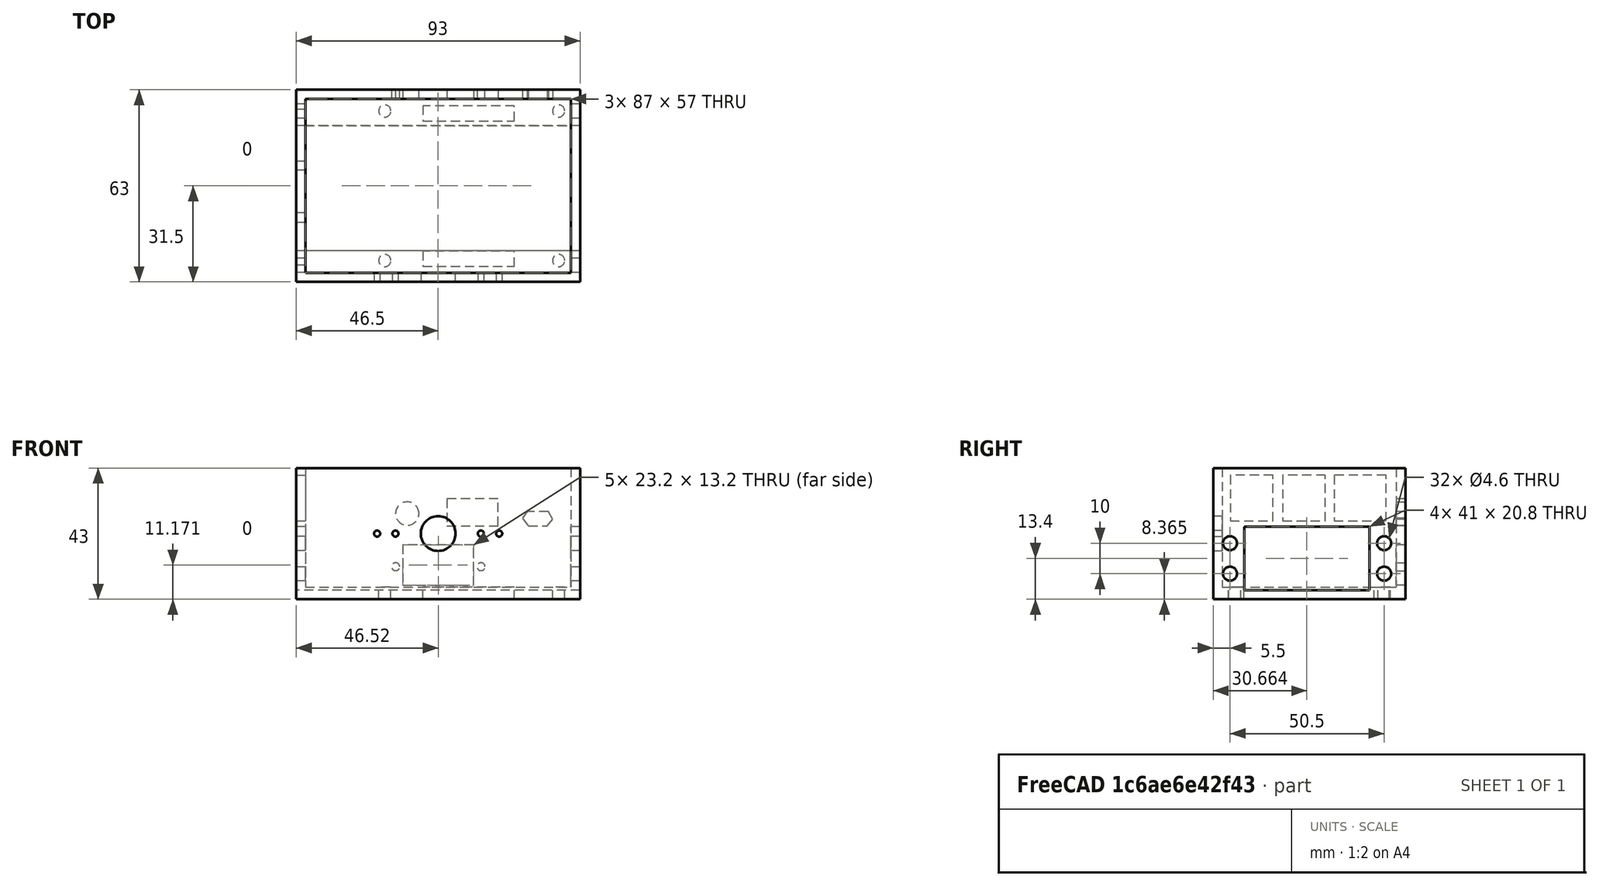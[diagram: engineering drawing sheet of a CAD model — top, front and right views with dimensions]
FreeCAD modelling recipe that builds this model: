
FCSTD DOCUMENT  (FreeCAD 0.17R8939 (Git))
Label: tronco
License: All rights reserved
LicenseURL: http://en.wikipedia.org/wiki/All_rights_reserved
objects: Sketcher::SketchObject×6, PartDesign::Pocket×6, Mesh::Feature×5, Part::Cylinder×4, App::MeasureDistance×3, App::DocumentObjectGroup×2, Part::Box×1, Part::MultiFuse×1, Part::Cut×1
note: 25 computed .brp shape members not serialized (recipe doc carries the construction recipe); baked Part::Feature solids carry a one-line shape summary decoded from their .brp

FEATURE [Mesh::Feature] rPi2_01
FEATURE [Mesh::Feature] Parallax_servo_repaired
  Placement = pos=(62,0,-22) rot=(0.57735,0.57735,0.57735;2.0944rad)
FEATURE [Mesh::Feature] Parallax_servo_repaired001
  Placement = pos=(22,0,-2) rot=(0.57735,0.57735,-0.57735;4.18879rad)
FEATURE [Mesh::Feature] Servo_SG90
  Placement = pos=(31,44,-7) rot=(-1,0,0;1.5708rad)
FEATURE [Part::Box] Box  label="Cubo"
  AttacherType = Attacher::AttachEngine3D
  Height = 43
  Length = 93
  Placement = pos=(-5,-3,-25) rot=(0,0,1;0rad)
  Width = 63
FEATURE [Sketcher::SketchObject] Sketch
  ExternalGeometry = -> [Box]
  MapMode = 5
  Placement = pos=(-5,-3,18) rot=(0,0,1;0rad)
  Support = -> [Box]
  sketch-geometry (4):
    g0: LineSegment StartX=3 StartY=60 StartZ=0 EndX=90 EndY=60 EndZ=0
    g1: LineSegment StartX=90 StartY=60 StartZ=0 EndX=90 EndY=3 EndZ=0
    g2: LineSegment StartX=90 StartY=3 StartZ=0 EndX=3 EndY=3 EndZ=0
    g3: LineSegment StartX=3 StartY=3 StartZ=0 EndX=3 EndY=60 EndZ=0
  constraints (12):
    c: Coincident(g0,g1)
    c: Coincident(g1,g2)
    c: Coincident(g2,g3)
    c: Coincident(g3,g0)
    c: Horizontal(g0)
    c: Horizontal(g2)
    c: Vertical(g1)
    c: Vertical(g3)
    c: Distance(g0,g-3) = 3
    c: Distance(g0,g-4) = 3
    c: DistanceY(g-1,g1) = 3
    c: DistanceX(g-2,g2) = 3
FEATURE [PartDesign::Pocket] Pocket  label="Puertos Multimedia"
  Length = 39
  Placement = pos=(-5,-3,-25) rot=(0,0,1;0rad)
  Profile = -> Sketch
  Type = 0
FEATURE [Sketcher::SketchObject] Sketch001
  ExternalGeometry = -> [Pocket]
  MapMode = 5
  Placement = pos=(-5,60,-25) rot=(0,0.707107,0.707107;3.14159rad)
  Support = -> [Pocket]
  sketch-geometry (18):
    g0: Circle CenterX=-36.37 CenterY=28.0687 CenterZ=0 NormalX=0 NormalY=0 NormalZ=1 Radius=3.84
    g1: LineSegment StartX=-66.2 StartY=32.9 StartZ=0 EndX=-49.42 EndY=32.9 EndZ=0
    g2: LineSegment StartX=-49.42 StartY=32.9 StartZ=0 EndX=-49.42 EndY=24.05 EndZ=0
    g3: LineSegment StartX=-49.42 StartY=24.05 StartZ=0 EndX=-66.2 EndY=24.05 EndZ=0
    g4: LineSegment StartX=-66.2 StartY=24.05 StartZ=0 EndX=-66.2 EndY=32.9 EndZ=0
    g5: LineSegment StartX=-82.6171 StartY=28.7 StartZ=0 EndX=-75.6871 EndY=28.7 EndZ=0
    g6: LineSegment StartX=-75.6871 StartY=28.7 StartZ=0 EndX=-74.1347 EndY=26.5182 EndZ=0
    g7: LineSegment StartX=-74.1347 StartY=26.5182 StartZ=0 EndX=-76.0497 EndY=24.0555 EndZ=0
    g8: LineSegment StartX=-76.0497 StartY=24.0555 StartZ=0 EndX=-82.2523 EndY=24.0555 EndZ=0
    g9: LineSegment StartX=-82.2523 StartY=24.0555 StartZ=0 EndX=-84.08 EndY=26.1498 EndZ=0
    g10: LineSegment StartX=-84.08 StartY=26.1498 StartZ=0 EndX=-82.6171 EndY=28.7 EndZ=0
    g11: LineSegment StartX=-58.12 StartY=17.7713 StartZ=0 EndX=-34.92 EndY=17.7713 EndZ=0
    g12: LineSegment StartX=-34.92 StartY=17.7713 StartZ=0 EndX=-34.92 EndY=4.57128 EndZ=0
    g13: LineSegment StartX=-34.92 StartY=4.57128 StartZ=0 EndX=-58.12 EndY=4.57128 EndZ=0
    g14: LineSegment StartX=-58.12 StartY=4.57128 StartZ=0 EndX=-58.12 EndY=17.7713 EndZ=0
    g15: Circle CenterX=-32.57 CenterY=10.65 CenterZ=0 NormalX=0 NormalY=0 NormalZ=1 Radius=1.3
    g16: Circle CenterX=-60.57 CenterY=10.65 CenterZ=0 NormalX=0 NormalY=0 NormalZ=1 Radius=1.3
    g17: LineSegment [constr] StartX=-93 StartY=10.65 StartZ=0 EndX=0 EndY=10.65 EndZ=0
  constraints (48):
    c: Coincident(g1,g2)
    c: Coincident(g2,g3)
    c: Coincident(g3,g4)
    c: Coincident(g4,g1)
    c: Horizontal(g1)
    c: Horizontal(g3)
    c: Vertical(g2)
    c: Vertical(g4)
    c: Horizontal(g5)
    c: Coincident(g5,g6)
    c: Coincident(g6,g7)
    c: Coincident(g7,g8)
    c: Horizontal(g8)
    c: Coincident(g8,g9)
    c: Coincident(g9,g10)
    c: Coincident(g10,g5)
    c: Coincident(g11,g12)
    c: Coincident(g12,g13)
    c: Coincident(g13,g14)
    c: Coincident(g14,g11)
    c: Horizontal(g11)
    c: Horizontal(g13)
    c: Vertical(g12)
    c: Vertical(g14)
    c: DistanceX(g13,g13) = 23.2
    c: DistanceY(g12,g12) = 13.2
    c: Horizontal(g17)
    c: PointOnObject(g16,g17)
    c: PointOnObject(g15,g17)
    c: Radius(g16) = 1.3
    c: Equal(g15,g16)
    c: PointOnObject(g17,g-2)
    c: PointOnObject(g17,g-3)
    c: Distance(g16,g15) = 28
    c: Distance(g9,g-3) = 8.92
    c: DistanceX(g5,g5) = 6.93
    c: Distance(g5,g9) = 2.94
    c: Distance(g5,g-4) = 14.3
    c: DistanceX(g1,g1) = 16.78
    c: DistanceY(g2,g2) = 8.85
    c: Distance(g1,g-4) = 10.1
    c: Distance(g3,g-3) = 26.8
    c: Radius(g0) = 3.84
    c: DistanceX(g-2,g0) = -36.37
    c: Distance(g13,g-3) = 34.88
    c: Distance(g15,g12) = 2.35
    c: Angle(g7,g8) = 2.23175
    c: Distance(g-1,g17) = 10.65
FEATURE [PartDesign::Pocket] Pocket001  label="Servomotores"
  Length = 5
  Placement = pos=(-5,-3,-25) rot=(0,0,1;0rad)
  Profile = -> Sketch001
  Type = 0
FEATURE [Sketcher::SketchObject] Sketch002
  ExternalGeometry = -> [Pocket001]
  MapMode = 5
  Placement = pos=(88,-3,-25) rot=(0.57735,0.57735,0.57735;2.0944rad)
  Support = -> [Pocket001]
  sketch-geometry (12):
    g0: LineSegment StartX=10.1642 StartY=23.8 StartZ=0 EndX=51.1642 EndY=23.8 EndZ=0
    g1: LineSegment StartX=51.1642 StartY=23.8 StartZ=0 EndX=51.1642 EndY=3 EndZ=0
    g2: LineSegment StartX=51.1642 StartY=3 StartZ=0 EndX=10.1642 EndY=3 EndZ=0
    g3: LineSegment StartX=10.1642 StartY=3 StartZ=0 EndX=10.1642 EndY=23.8 EndZ=0
    g4: Circle CenterX=56 CenterY=18.3651 CenterZ=0 NormalX=0 NormalY=0 NormalZ=1 Radius=2.3
    g5: Circle CenterX=56 CenterY=8.36507 CenterZ=0 NormalX=0 NormalY=0 NormalZ=1 Radius=2.3
    g6: Circle CenterX=5.5 CenterY=18.3651 CenterZ=0 NormalX=0 NormalY=0 NormalZ=1 Radius=2.3
    g7: Circle CenterX=5.5 CenterY=8.36507 CenterZ=0 NormalX=0 NormalY=0 NormalZ=1 Radius=2.3
    g8: LineSegment [constr] StartX=5.5 StartY=18.3651 StartZ=0 EndX=56 EndY=18.3651 EndZ=0
    g9: LineSegment [constr] StartX=56 StartY=18.3651 StartZ=0 EndX=56 EndY=8.36507 EndZ=0
    g10: LineSegment [constr] StartX=56 StartY=8.36507 StartZ=0 EndX=5.5 EndY=8.36507 EndZ=0
    g11: LineSegment [constr] StartX=5.5 StartY=8.36507 StartZ=0 EndX=5.5 EndY=18.3651 EndZ=0
  constraints (32):
    c: Coincident(g0,g1)
    c: Coincident(g1,g2)
    c: Coincident(g2,g3)
    c: Coincident(g3,g0)
    c: Horizontal(g0)
    c: Horizontal(g2)
    c: Vertical(g1)
    c: Vertical(g3)
    c: DistanceX(g0,g0) = 41
    c: DistanceY(g1,g1) = 20.8
    c: Radius(g5) = 2.3
    c: Equal(g5,g4)
    c: Equal(g4,g6)
    c: Equal(g6,g7)
    c: Coincident(g8,g9)
    c: Coincident(g9,g10)
    c: Coincident(g10,g11)
    c: Coincident(g11,g8)
    c: Horizontal(g8)
    c: Horizontal(g10)
    c: Vertical(g9)
    c: Vertical(g11)
    c: Coincident(g7,g10)
    c: Coincident(g6,g8)
    c: Coincident(g4,g8)
    c: Coincident(g5,g9)
    c: DistanceX(g10,g10) = 50.5
    c: DistanceY(g11,g11) = 10
    c: DistanceY(g-1,g7) = 8.36507
    c: Distance(g4,g-3) = 7
    c: DistanceY(g-1,g1) = 3
    c: Distance(g0,g-3) = 11.8358
FEATURE [PartDesign::Pocket] Pocket002  label="puertosUSB"
  Length = 5
  Placement = pos=(-5,-3,-25) rot=(0,0,1;0rad)
  Profile = -> Sketch002
  Type = 1
FEATURE [Sketcher::SketchObject] Sketch003
  ExternalGeometry = -> [Pocket002]
  MapMode = 5
  Placement = pos=(-5,-3,-25) rot=(0.57735,-0.57735,-0.57735;2.0944rad)
  Support = -> [Pocket002]
  sketch-geometry (13):
    g0: LineSegment StartX=-19.56 StartY=40.62 StartZ=0 EndX=-5.56 EndY=40.62 EndZ=0
    g1: LineSegment StartX=-5.56 StartY=40.62 StartZ=0 EndX=-5.56 EndY=25.62 EndZ=0
    g2: LineSegment StartX=-5.56 StartY=25.62 StartZ=0 EndX=-19.56 EndY=25.62 EndZ=0
    g3: LineSegment StartX=-19.56 StartY=25.62 StartZ=0 EndX=-19.56 EndY=40.62 EndZ=0
    g4: LineSegment StartX=-36.75 StartY=40.62 StartZ=0 EndX=-22.75 EndY=40.62 EndZ=0
    g5: LineSegment StartX=-22.75 StartY=40.62 StartZ=0 EndX=-22.75 EndY=25.62 EndZ=0
    g6: LineSegment StartX=-22.75 StartY=25.62 StartZ=0 EndX=-36.75 EndY=25.62 EndZ=0
    g7: LineSegment StartX=-36.75 StartY=25.62 StartZ=0 EndX=-36.75 EndY=40.62 EndZ=0
    g8: LineSegment StartX=-56.62 StartY=40.62 StartZ=0 EndX=-39.62 EndY=40.62 EndZ=0
    g9: LineSegment StartX=-39.62 StartY=40.62 StartZ=0 EndX=-39.62 EndY=25.62 EndZ=0
    g10: LineSegment StartX=-39.62 StartY=25.62 StartZ=0 EndX=-56.62 EndY=25.62 EndZ=0
    g11: LineSegment StartX=-56.62 StartY=25.62 StartZ=0 EndX=-56.62 EndY=40.62 EndZ=0
    g12: LineSegment [constr] StartX=-63 StartY=25.62 StartZ=0 EndX=0 EndY=25.62 EndZ=0
  constraints (42):
    c: Coincident(g0,g1)
    c: Coincident(g1,g2)
    c: Coincident(g2,g3)
    c: Coincident(g3,g0)
    c: Horizontal(g0)
    c: Horizontal(g2)
    c: Vertical(g1)
    c: Vertical(g3)
    c: Coincident(g4,g5)
    c: Coincident(g5,g6)
    c: Coincident(g6,g7)
    c: Coincident(g7,g4)
    c: Horizontal(g4)
    c: Horizontal(g6)
    c: Vertical(g5)
    c: Vertical(g7)
    c: Coincident(g8,g9)
    c: Coincident(g9,g10)
    c: Coincident(g10,g11)
    c: Coincident(g11,g8)
    c: Horizontal(g8)
    c: Horizontal(g10)
    c: Vertical(g9)
    c: Vertical(g11)
    c: DistanceY(g1,g1) = 15
    c: DistanceX(g0,g0) = 14
    c: DistanceX(g8,g8) = 17
    c: Equal(g4,g0)
    c: Equal(g9,g7)
    c: Equal(g7,g11)
    c: Equal(g11,g3)
    c: Equal(g3,g1)
    c: Horizontal(g12)
    c: PointOnObject(g12,g-2)
    c: PointOnObject(g12,g-3)
    c: PointOnObject(g10,g12)
    c: PointOnObject(g6,g12)
    c: PointOnObject(g2,g12)
    c: Distance(g4,g0) = 3.19
    c: Distance(g8,g4) = 2.87
    c: Distance(g-3,g12) = 17.38
    c: Distance(g12,g10) = 6.38
FEATURE [PartDesign::Pocket] Pocket003
  Length = 5
  Placement = pos=(-5,-3,-25) rot=(0,0,1;0rad)
  Profile = -> Sketch003
  Type = 0
FEATURE [Part::Cylinder] Cylinder  label="Cilindro"
  Angle = 360
  AttacherType = Attacher::AttachEngine3D
  Height = 40
  Placement = pos=(24,4,-27) rot=(0,0,1;0rad)
  Radius = 2
FEATURE [Part::Cylinder] Cylinder001  label="Cilindro001"
  Angle = 360
  AttacherType = Attacher::AttachEngine3D
  Height = 40
  Placement = pos=(81,4,-27) rot=(0,0,1;0rad)
  Radius = 2
FEATURE [Part::Cylinder] Cylinder002  label="Cilindro002"
  Angle = 360
  AttacherType = Attacher::AttachEngine3D
  Height = 40
  Placement = pos=(81,53,-27) rot=(0,0,1;0rad)
  Radius = 2
FEATURE [Part::Cylinder] Cylinder003  label="Cilindro003"
  Angle = 360
  AttacherType = Attacher::AttachEngine3D
  Height = 40
  Placement = pos=(24,53,-27) rot=(0,0,1;0rad)
  Radius = 2
FEATURE [Part::MultiFuse] Fusion
  Shapes = -> [Cylinder003,Cylinder,Cylinder002,Cylinder001]
FEATURE [Part::Cut] Cut  label="soportes Pi"
  Base = -> Pocket003
  Tool = -> Fusion
FEATURE [Sketcher::SketchObject] Sketch004
  ExternalGeometry = -> [Cut]
  MapMode = 5
  Placement = pos=(0,-3,0) rot=(1,0,0;1.5708rad)
  Support = -> [Cut]
  sketch-geometry (8):
    g0: LineSegment [constr] StartX=-5 StartY=18 StartZ=0 EndX=88 EndY=-25 EndZ=0
    g1: LineSegment [constr] StartX=88 StartY=18 StartZ=0 EndX=-5 EndY=-25 EndZ=0
    g2: Circle CenterX=41.5 CenterY=-3.5 CenterZ=0 NormalX=0 NormalY=0 NormalZ=1 Radius=5.7
    g3: LineSegment [constr] StartX=-5 StartY=-3.5 StartZ=0 EndX=88 EndY=-3.5 EndZ=0
    g4: Circle CenterX=21.5 CenterY=-3.5 CenterZ=0 NormalX=0 NormalY=0 NormalZ=1 Radius=1
    g5: Circle CenterX=27.5 CenterY=-3.5 CenterZ=0 NormalX=0 NormalY=0 NormalZ=1 Radius=1
    g6: Circle CenterX=55.5 CenterY=-3.5 CenterZ=0 NormalX=0 NormalY=0 NormalZ=1 Radius=1
    g7: Circle CenterX=61.5 CenterY=-3.5 CenterZ=0 NormalX=0 NormalY=0 NormalZ=1 Radius=1
  constraints (23):
    c: Coincident(g1,g-6)
    c: Coincident(g0,g-4)
    c: Coincident(g1,g-5)
    c: Coincident(g0,g-6)
    c: PointOnObject(g2,g1)
    c: PointOnObject(g2,g0)
    c: Radius(g2) = 5.7
    c: Horizontal(g3)
    c: PointOnObject(g3,g-6)
    c: PointOnObject(g3,g-3)
    c: PointOnObject(g2,g3)
    c: PointOnObject(g4,g3)
    c: PointOnObject(g5,g3)
    c: PointOnObject(g6,g3)
    c: PointOnObject(g7,g3)
    c: Radius(g4) = 1
    c: Equal(g4,g5)
    c: Equal(g5,g6)
    c: Equal(g6,g7)
    c: Distance(g2,g6) = 14
    c: Distance(g6,g7) = 6
    c: Distance(g2,g5) = 14
    c: Distance(g5,g4) = 6
FEATURE [PartDesign::Pocket] Pocket004  label="tronco"
  Length = 5
  Profile = -> Sketch004
  Type = 0
FEATURE [App::DocumentObjectGroup] Grupo  label="Montaje"
  Group = -> [rPi2_01,Parallax_servo_repaired,Parallax_servo_repaired001,Servo_SG90]
FEATURE [Sketcher::SketchObject] Sketch005
  ExternalGeometry = -> [Pocket004]
  MapMode = 5
  Placement = pos=(0,0,-25) rot=(1,0,0;3.14159rad)
  Support = -> [Pocket004]
  sketch-geometry (9):
    g0: LineSegment StartX=36.4989 StartY=-49.73 StartZ=0 EndX=66.4989 EndY=-49.73 EndZ=0
    g1: LineSegment StartX=66.4989 StartY=-49.73 StartZ=0 EndX=66.4989 EndY=-54.73 EndZ=0
    g2: LineSegment StartX=66.4989 StartY=-54.73 StartZ=0 EndX=36.4989 EndY=-54.73 EndZ=0
    g3: LineSegment StartX=36.4989 StartY=-54.73 StartZ=0 EndX=36.4989 EndY=-49.73 EndZ=0
    g4: LineSegment StartX=36.4989 StartY=-2.08 StartZ=0 EndX=66.4989 EndY=-2.08 EndZ=0
    g5: LineSegment StartX=66.4989 StartY=-2.08 StartZ=0 EndX=66.4989 EndY=-7.08 EndZ=0
    g6: LineSegment StartX=66.4989 StartY=-7.08 StartZ=0 EndX=36.4989 EndY=-7.08 EndZ=0
    g7: LineSegment StartX=36.4989 StartY=-7.08 StartZ=0 EndX=36.4989 EndY=-2.08 EndZ=0
    g8: LineSegment [constr] StartX=66.4989 StartY=3 StartZ=0 EndX=66.4989 EndY=-60 EndZ=0
  constraints (27):
    c: Coincident(g0,g1)
    c: Coincident(g1,g2)
    c: Coincident(g2,g3)
    c: Coincident(g3,g0)
    c: Horizontal(g0)
    c: Horizontal(g2)
    c: Vertical(g1)
    c: Vertical(g3)
    c: Coincident(g4,g5)
    c: Coincident(g5,g6)
    c: Coincident(g6,g7)
    c: Coincident(g7,g4)
    c: Horizontal(g4)
    c: Horizontal(g6)
    c: Vertical(g5)
    c: Vertical(g7)
    c: DistanceX(g6,g6) = 30
    c: Equal(g0,g6)
    c: DistanceY(g3,g3) = 5
    c: Equal(g7,g3)
    c: Vertical(g8)
    c: PointOnObject(g8,g-4)
    c: PointOnObject(g8,g-3)
    c: PointOnObject(g0,g8)
    c: PointOnObject(g4,g8)
    c: Distance(g5,g0) = 42.65
    c: Distance(g2,g-3) = 5.27
FEATURE [PartDesign::Pocket] Pocket005  label="pasacables"
  Length = 5
  Profile = -> Sketch005
  Type = 0
FEATURE [App::DocumentObjectGroup] Grupo001  label="Tronco"
  Group = -> [Box,Pocket,Pocket001,Pocket002,Cut,Pocket004,Pocket005]
FEATURE [Mesh::Feature] Servo_SG091
  Placement = pos=(32,71,0) rot=(0,1,0;1.5708rad)
FEATURE [App::MeasureDistance] Distance  label="Distance: 93,00 mm"
  Distance = 93
  P1 = (-5,60,18)
  P2 = (88,60,18)
FEATURE [App::MeasureDistance] Distance001  label="Distance: 43,00 mm"
  Distance = 43
  P1 = (-5,60,-25)
  P2 = (-5,60,18)
FEATURE [App::MeasureDistance] Distance002  label="Distance: 63,00 mm"
  Distance = 63
  P1 = (-5,60,18)
  P2 = (-5,-3,18)
